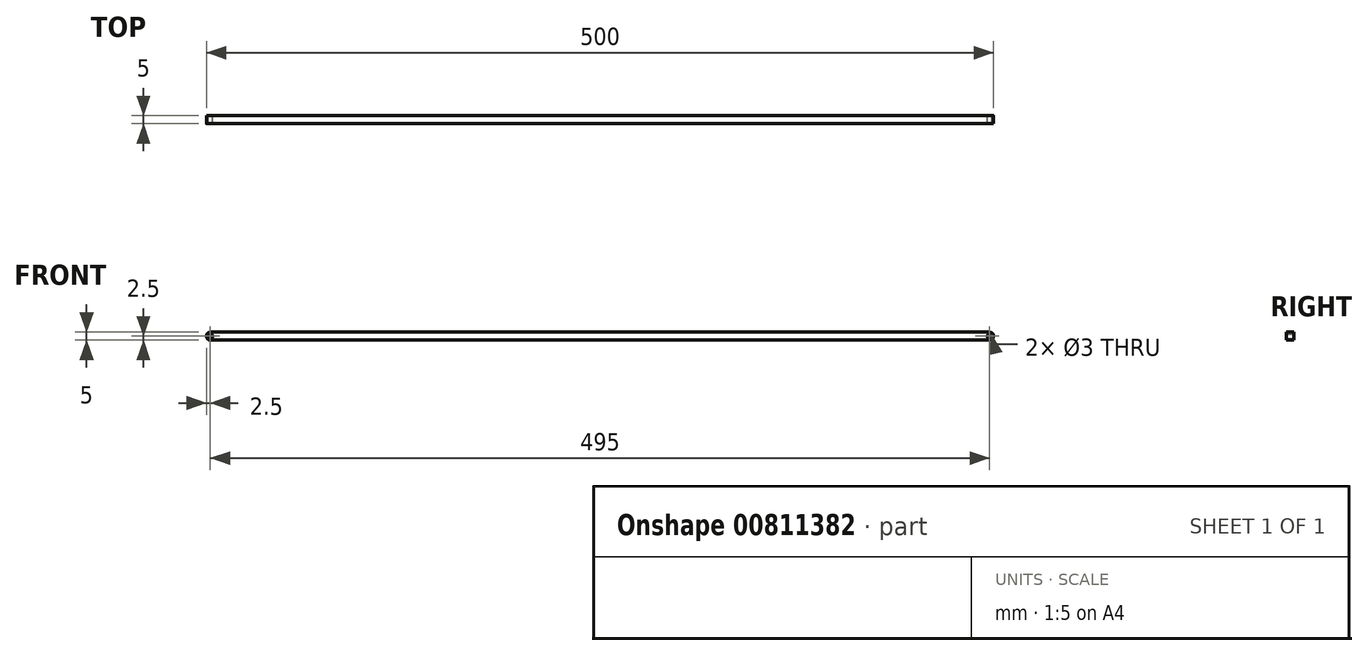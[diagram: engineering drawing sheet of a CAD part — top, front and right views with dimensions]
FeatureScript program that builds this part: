
annotation { "Feature Type Name" : "Feature", "Feature Type Description" : "" }
export const myFeature = defineFeature(function(context is Context, id is Id, definition is map)
    precondition{}
    {
        {
            var Q0;
            Q0=qCreatedBy(makeId("Front.planeOp"),FACE);
            var sketch = newSketch(context, id + "F0", { "sketchPlane" : qUnion([Q0])});
            skLineSegment(sketch, "E0.bottom", {"start": v(250, -2.5) * mm, "end": v(-250, -2.5) * mm});
            skLineSegment(sketch, "E0.top", {"start": v(250, 2.5) * mm, "end": v(-250, 2.5) * mm});
            skLineSegment(sketch, "E0.left", {"start": v(250, -2.5) * mm, "end": v(250, 2.5) * mm});
            skLineSegment(sketch, "E0.right", {"start": v(-250, -2.5) * mm, "end": v(-250, 2.5) * mm});
            skPoint(sketch, "E0.middle", {"position": v(0, 0) * mm});
            skCircle(sketch, "E1", {"center": v(-247.5, 0) * mm, "radius": 1.5 * mm});
            skPoint(sketch, "E1.centerSnap0", {"position": v(-250, 0) * mm});
            skCircle(sketch, "E2", {"center": v(247.5, 0) * mm, "radius": 1.5 * mm});
            skPoint(sketch, "E2.centerSnap0", {"position": v(250, 0) * mm});
            skSolve(sketch);
        }
        {
            var Q0;
            Q0=makeQuery(id+"F0.imprint","IMPRINT",FACE,{"disambiguationData":[TD([[makeQuery(id+"F0.imprint","IMPRINT",EDGE,{"derivedFrom":sQuery(id+"F0.wireOp",EDGE,"E0.bottom")}),-1.0]])]});
            extrude(context, id + "F1", {"entities" : qUnion([Q0]), "depth" : 5 * mm, "offsetDistance" : 25 * mm});
        }
        {
            var Q0;
            Q0=makeQuery(id+"F1.opExtrude","SWEPT_EDGE",EDGE,{"disambiguationData":[OSD([sQuery(id+"F0.wireOp",EDGE,"E0.top"),sQuery(id+"F0.wireOp",EDGE,"E0.left")])]});
            var Q1;
            Q1=makeQuery(id+"F1.opExtrude","SWEPT_EDGE",EDGE,{"disambiguationData":[OSD([sQuery(id+"F0.wireOp",EDGE,"E0.bottom"),sQuery(id+"F0.wireOp",EDGE,"E0.left")])]});
            var Q2;
            Q2=makeQuery(id+"F1.opExtrude","SWEPT_EDGE",EDGE,{"disambiguationData":[OSD([sQuery(id+"F0.wireOp",EDGE,"E0.top"),sQuery(id+"F0.wireOp",EDGE,"E0.right")])]});
            var Q3;
            Q3=makeQuery(id+"F1.opExtrude","SWEPT_EDGE",EDGE,{"disambiguationData":[OSD([sQuery(id+"F0.wireOp",EDGE,"E0.bottom"),sQuery(id+"F0.wireOp",EDGE,"E0.right")])]});
            fillet(context, id + "F2", {"entities" : qUnion([Q0, Q1, Q2, Q3]), "radius" : 2.5 * mm, "tangentPropagation" : true, "allowEdgeOverflow" : false});
        }
    });
